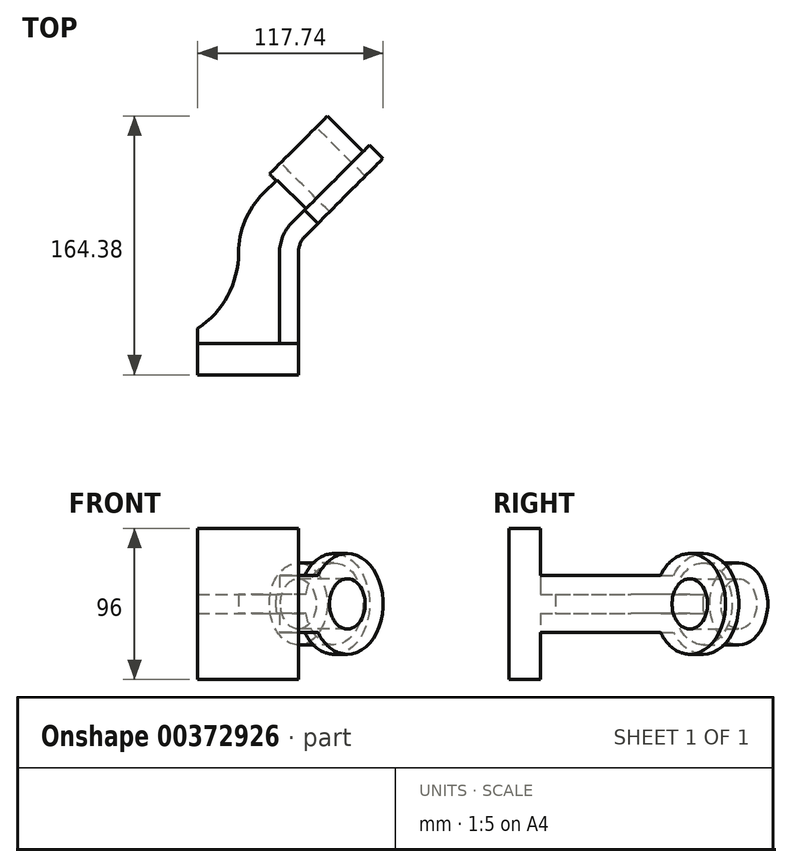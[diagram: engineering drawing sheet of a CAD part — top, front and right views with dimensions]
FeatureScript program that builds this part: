
annotation { "Feature Type Name" : "Feature", "Feature Type Description" : "" }
export const myFeature = defineFeature(function(context is Context, id is Id, definition is map)
    precondition{}
    {
        {
            var Q0;
            Q0=qCreatedBy(makeId("Top.planeOp"),FACE);
            var sketch = newSketch(context, id + "F0", { "sketchPlane" : qUnion([Q0])});
            skLineSegment(sketch, "E0", {"start": v(0, 0) * mm, "end": v(64, 0) * mm});
            skLineSegment(sketch, "E1", {"start": v(82.38, 164.38) * mm, "end": v(64, 146) * mm});
            skPoint(sketch, "E2", {"position": v(64, 146) * mm});
            skLineSegment(sketch, "E3", {"start": v(82.38, 164.38) * mm, "end": v(105.01, 141.76) * mm});
            skLineSegment(sketch, "E4", {"start": v(109.25, 146) * mm, "end": v(86.63, 123.37) * mm});
            skLineSegment(sketch, "E5", {"start": v(64, 146) * mm, "end": v(31.84, 146) * mm, "construction": true});
            skLineSegment(sketch, "E6", {"start": v(109.25, 146) * mm, "end": v(117.74, 137.51) * mm});
            skLineSegment(sketch, "E7", {"start": v(117.74, 137.51) * mm, "end": v(95.11, 114.89) * mm});
            skLineSegment(sketch, "E8", {"start": v(75.31, 157.31) * mm, "end": v(106.43, 126.2) * mm});
            skLineSegment(sketch, "E9", {"start": v(64, 146) * mm, "end": v(116.68, 93.32) * mm, "construction": true});
            skSolve(sketch);
        }
        {
            var Q0;
            Q0 = qSketchRegion(id + "F0", true);
            var Q1;
            Q1=sQuery(id+"F0.wireOp",EDGE,"E9");
            revolve(context, id + "F1", {"entities" : qUnion([Q0]), "axis" : qUnion([Q1]), "revolveType" : RevolveType.FULL});
        }
        {
            var Q0;
            Q0=qCreatedBy(makeId("Top.planeOp"),FACE);
            var sketch = newSketch(context, id + "F2", { "sketchPlane" : qUnion([Q0])});
            skLineSegment(sketch, "E10", {"start": v(64, 20) * mm, "end": v(64, 77.56) * mm});
            skLineSegment(sketch, "E11.0", {"start": v(52, 20) * mm, "end": v(52, 77.56) * mm});
            skLineSegment(sketch, "E12.0", {"start": v(72.49, 92.26) * mm, "end": v(117.74, 137.51) * mm});
            skLineSegment(sketch, "E13", {"start": v(76.8, 96.58) * mm, "end": v(68.4, 88.17) * mm});
            skArc(sketch, "E14.filletArc", {"start": v(68.4, 88.17) * mm, "mid": v(65.14, 83.3) * mm, "end": v(64, 77.56) * mm});
            skLineSegment(sketch, "E15.0", {"start": v(64, 100.75) * mm, "end": v(109.25, 146) * mm});
            skLineSegment(sketch, "E16", {"start": v(68.32, 105.06) * mm, "end": v(59.9, 96.65) * mm});
            skArc(sketch, "E17", {"start": v(59.9, 96.65) * mm, "mid": v(54.06, 87.9) * mm, "end": v(52, 77.56) * mm});
            skLineSegment(sketch, "E18", {"start": v(52, 20) * mm, "end": v(64, 20) * mm});
            skLineSegment(sketch, "E19", {"start": v(68.32, 105.06) * mm, "end": v(76.8, 96.58) * mm});
            skSolve(sketch);
        }
        {
            var Q0;
            Q0=makeQuery(id+"F2.imprint","IMPRINT",FACE,{"disambiguationData":[TD([[makeQuery(id+"F2.imprint","IMPRINT",EDGE,{"derivedFrom":sQuery(id+"F2.wireOp",EDGE,"E10")}),1.0]])]});
            extrude(context, id + "F3", {"entities" : qUnion([Q0]), "operationType" : NewBodyOperationType.ADD, "endBound" : BoundingType.SYMMETRIC, "depth" : 36 * mm});
        }
        {
            var Q0;
            Q0=qCreatedBy(makeId("Top.planeOp"),FACE);
            var sketch = newSketch(context, id + "F4", { "sketchPlane" : qUnion([Q0])});
            skLineSegment(sketch, "E20.0", {"start": v(52, 20) * mm, "end": v(64, 20) * mm});
            skLineSegment(sketch, "E21.bottom", {"start": v(0, 0) * mm, "end": v(64, 0) * mm});
            skLineSegment(sketch, "E21.top", {"start": v(0, 20) * mm, "end": v(64, 20) * mm});
            skLineSegment(sketch, "E21.left", {"start": v(0, 0) * mm, "end": v(0, 20) * mm});
            skLineSegment(sketch, "E21.right", {"start": v(64, 0) * mm, "end": v(64, 20) * mm});
            skSolve(sketch);
        }
        {
            var Q0;
            Q0=makeQuery(id+"F4.imprint","IMPRINT",FACE,{"disambiguationData":[TD([[makeQuery(id+"F4.imprint","IMPRINT",EDGE,{"derivedFrom":sQuery(id+"F4.wireOp",EDGE,"E21.bottom")}),1.0]])]});
            extrude(context, id + "F5", {"entities" : qUnion([Q0]), "operationType" : NewBodyOperationType.ADD, "endBound" : BoundingType.SYMMETRIC, "depth" : 96 * mm});
        }
        {
            var Q0;
            Q0=qCreatedBy(makeId("Top.planeOp"),FACE);
            var sketch = newSketch(context, id + "F6", { "sketchPlane" : qUnion([Q0])});
            skLineSegment(sketch, "E22", {"start": v(49.86, 123.37) * mm, "end": v(41.52, 115.04) * mm});
            skArc(sketch, "E23", {"start": v(41.52, 115.04) * mm, "mid": v(30.03, 97.84) * mm, "end": v(26, 77.56) * mm});
            skArc(sketch, "E24", {"start": v(0, 29.42) * mm, "mid": v(19.08, 50.2) * mm, "end": v(26, 77.56) * mm});
            skLineSegment(sketch, "E25", {"start": v(0, 20) * mm, "end": v(0, 29.42) * mm});
            skLineSegment(sketch, "E26.0", {"start": v(0, 20) * mm, "end": v(52, 20) * mm});
            skLineSegment(sketch, "E27.0", {"start": v(52, 20) * mm, "end": v(52, 77.56) * mm});
            skPoint(sketch, "E28.0", {"position": v(54.06, 87.9) * mm});
            skArc(sketch, "E29.0", {"start": v(59.9, 96.65) * mm, "mid": v(54.06, 87.9) * mm, "end": v(52, 77.56) * mm});
            skLineSegment(sketch, "E30.0", {"start": v(67.92, 104.66) * mm, "end": v(59.9, 96.65) * mm});
            skPoint(sketch, "E31.orphan", {"position": v(64, 20) * mm});
            skLineSegment(sketch, "E32", {"start": v(49.86, 123.37) * mm, "end": v(52.24, 125.76) * mm});
            skLineSegment(sketch, "E33", {"start": v(67.92, 104.66) * mm, "end": v(71.02, 107.73) * mm});
            skLineSegment(sketch, "E34", {"start": v(71.02, 107.73) * mm, "end": v(52.24, 125.76) * mm});
            skSolve(sketch);
        }
        {
            var Q0;
            Q0=makeQuery(id+"F6.imprint","IMPRINT",FACE,{"disambiguationData":[TD([[makeQuery(id+"F6.imprint","IMPRINT",EDGE,{"derivedFrom":sQuery(id+"F6.wireOp",EDGE,"E22")}),1.0]])]});
            extrude(context, id + "F7", {"entities" : qUnion([Q0]), "operationType" : NewBodyOperationType.ADD, "endBound" : BoundingType.SYMMETRIC, "depth" : 12 * mm});
        }
    });
